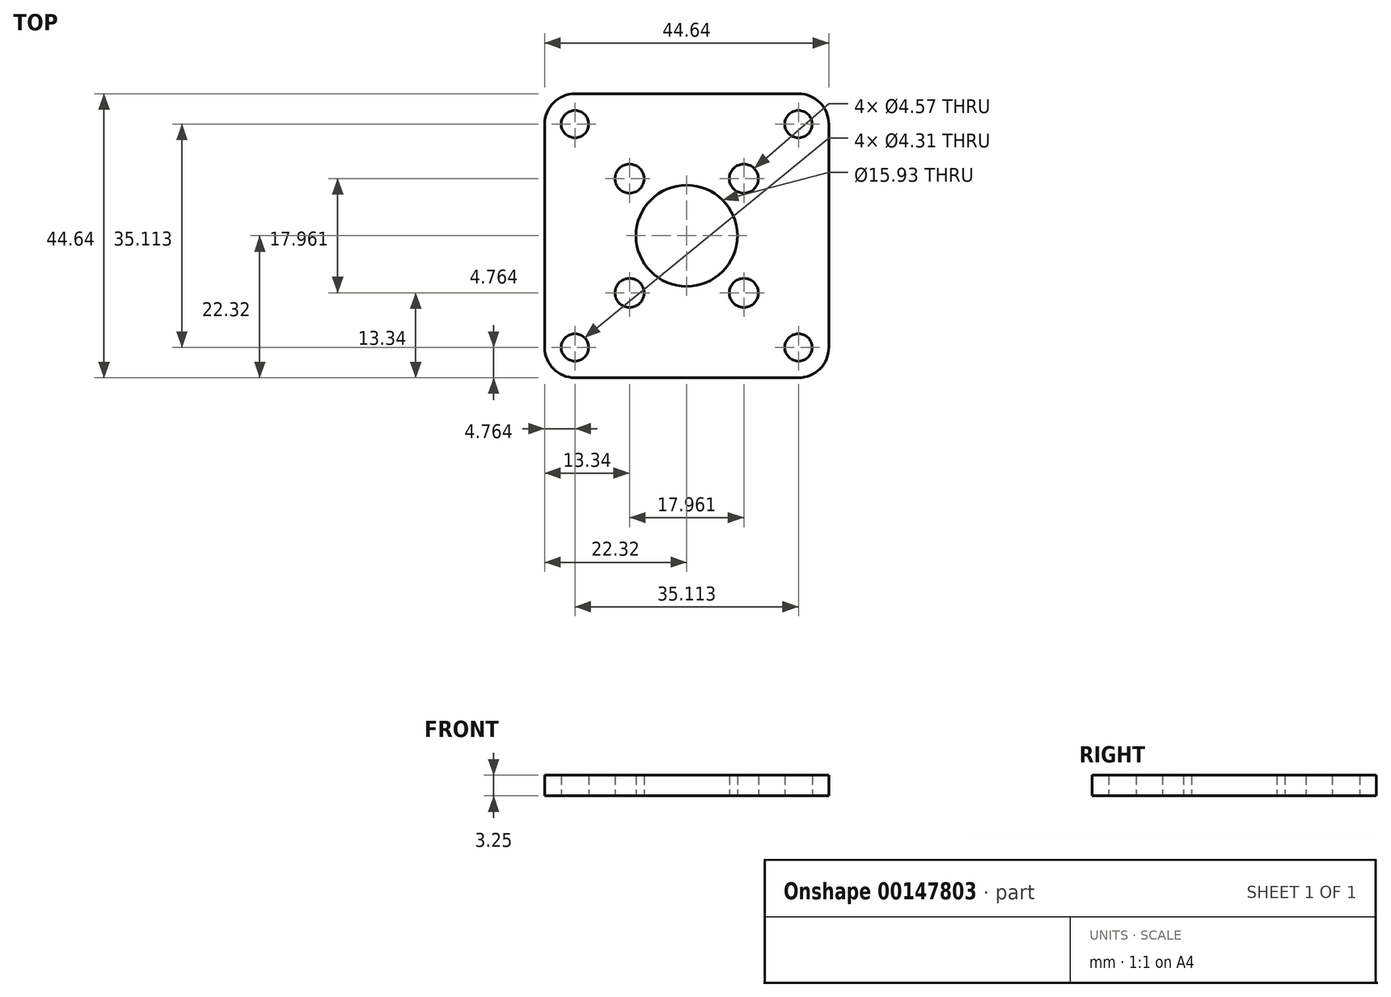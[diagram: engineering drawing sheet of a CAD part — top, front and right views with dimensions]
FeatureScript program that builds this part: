
annotation { "Feature Type Name" : "Feature", "Feature Type Description" : "" }
export const myFeature = defineFeature(function(context is Context, id is Id, definition is map)
    precondition{}
    {
        {
            var Q0;
            Q0=qCreatedBy(makeId("Top.planeOp"),FACE);
            var sketch = newSketch(context, id + "F0", { "sketchPlane" : qUnion([Q0])});
            skLineSegment(sketch, "E0.bottom", {"start": v(8.98, -8.98) * mm, "end": v(-8.98, -8.98) * mm, "construction": true});
            skLineSegment(sketch, "E0.top", {"start": v(8.98, 8.98) * mm, "end": v(-8.98, 8.98) * mm, "construction": true});
            skLineSegment(sketch, "E0.left", {"start": v(8.98, -8.98) * mm, "end": v(8.98, 8.98) * mm, "construction": true});
            skLineSegment(sketch, "E0.right", {"start": v(-8.98, -8.98) * mm, "end": v(-8.98, 8.98) * mm, "construction": true});
            skPoint(sketch, "E0.middle", {"position": v(0, 0) * mm});
            skCircle(sketch, "E1", {"center": v(-8.98, 8.98) * mm, "radius": 2.29 * mm});
            skCircle(sketch, "E2", {"center": v(-8.98, -8.98) * mm, "radius": 2.29 * mm});
            skCircle(sketch, "E3", {"center": v(8.98, -8.98) * mm, "radius": 2.29 * mm});
            skCircle(sketch, "E4", {"center": v(8.98, 8.98) * mm, "radius": 2.29 * mm});
            skCircle(sketch, "E5", {"center": v(0, 0) * mm, "radius": 20.07 * mm, "construction": true});
            skLineSegment(sketch, "E6.bottom", {"start": v(17.56, 17.56) * mm, "end": v(-17.56, 17.56) * mm, "construction": true});
            skLineSegment(sketch, "E6.top", {"start": v(17.56, -17.56) * mm, "end": v(-17.56, -17.56) * mm, "construction": true});
            skLineSegment(sketch, "E6.left", {"start": v(17.56, 17.56) * mm, "end": v(17.56, -17.56) * mm, "construction": true});
            skLineSegment(sketch, "E6.right", {"start": v(-17.56, 17.56) * mm, "end": v(-17.56, -17.56) * mm, "construction": true});
            skCircle(sketch, "E7", {"center": v(-17.56, 17.56) * mm, "radius": 2.15 * mm});
            skCircle(sketch, "E8", {"center": v(17.56, 17.56) * mm, "radius": 2.15 * mm});
            skCircle(sketch, "E9", {"center": v(17.56, -17.56) * mm, "radius": 2.15 * mm});
            skCircle(sketch, "E10", {"center": v(-17.56, -17.56) * mm, "radius": 2.15 * mm});
            skCircle(sketch, "E11", {"center": v(17.56, 17.56) * mm, "radius": 4.76 * mm, "construction": true});
            skLineSegment(sketch, "E12.bottom", {"start": v(22.32, -22.32) * mm, "end": v(-22.32, -22.32) * mm});
            skLineSegment(sketch, "E12.top", {"start": v(22.32, 22.32) * mm, "end": v(-22.32, 22.32) * mm});
            skLineSegment(sketch, "E12.left", {"start": v(22.32, -22.32) * mm, "end": v(22.32, 22.32) * mm});
            skLineSegment(sketch, "E12.right", {"start": v(-22.32, -22.32) * mm, "end": v(-22.32, 22.32) * mm});
            skCircle(sketch, "E13", {"center": v(0, 0) * mm, "radius": 7.96 * mm});
            skSolve(sketch);
        }
        {
            var Q0;
            Q0=qSketchRegion(id+"F0",true);
            extrude(context, id + "F1", {"entities" : qUnion([Q0]), "depth" : 3.25 * mm});
        }
        {
            var Q0;
            Q0=makeQuery(id+"F1.opExtrude","SWEPT_EDGE",EDGE,{"disambiguationData":[OSD([sQuery(id+"F0.wireOp",EDGE,"E12.bottom"),sQuery(id+"F0.wireOp",EDGE,"E12.right")])]});
            var Q1;
            Q1=makeQuery(id+"F1.opExtrude","SWEPT_EDGE",EDGE,{"disambiguationData":[OSD([sQuery(id+"F0.wireOp",EDGE,"E12.bottom"),sQuery(id+"F0.wireOp",EDGE,"E12.left")])]});
            var Q2;
            Q2=makeQuery(id+"F1.opExtrude","SWEPT_EDGE",EDGE,{"disambiguationData":[OSD([sQuery(id+"F0.wireOp",EDGE,"E12.top"),sQuery(id+"F0.wireOp",EDGE,"E12.left")])]});
            var Q3;
            Q3=makeQuery(id+"F1.opExtrude","SWEPT_EDGE",EDGE,{"disambiguationData":[OSD([sQuery(id+"F0.wireOp",EDGE,"E12.top"),sQuery(id+"F0.wireOp",EDGE,"E12.right")])]});
            fillet(context, id + "F2", {"entities" : qUnion([Q0, Q1, Q2, Q3]), "radius" : 4.76 * mm, "tangentPropagation" : true, "allowEdgeOverflow" : false});
        }
    });
